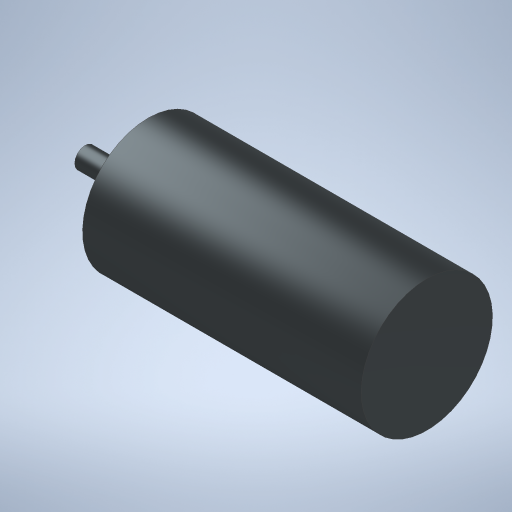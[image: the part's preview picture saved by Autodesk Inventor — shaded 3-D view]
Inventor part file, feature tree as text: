
AUTODESK INVENTOR PART (.ipt)
format: ipt  version: 2023 (Build 270158000, 158)  size: 231,424 bytes
history: native  units: mm
features: extrude x2, sketch x2, plane x1
ambient origin geometry x8: Origin, YZ Plane, XZ Plane, XY Plane, X Axis, Y Axis, Z Axis, Center Point
bodies: Volumenkörper1 (feature_tree)
feature tree (5):
  extrude  "Extrusion1"  Depth=53.0mm TaperAngle=0.0deg
  extrude  "Extrusion2"  Depth=12.0mm TaperAngle=0.0deg
  plane  "Arbeitsebene2"
  sketch  "Skizze2"  dims[d0=25.0mm d1=53.0mm d2=0.0mm]
  sketch  "Skizze3"  dims[d3=4.0mm d4=12.0mm d5=0.0mm d6=0.0mm]
